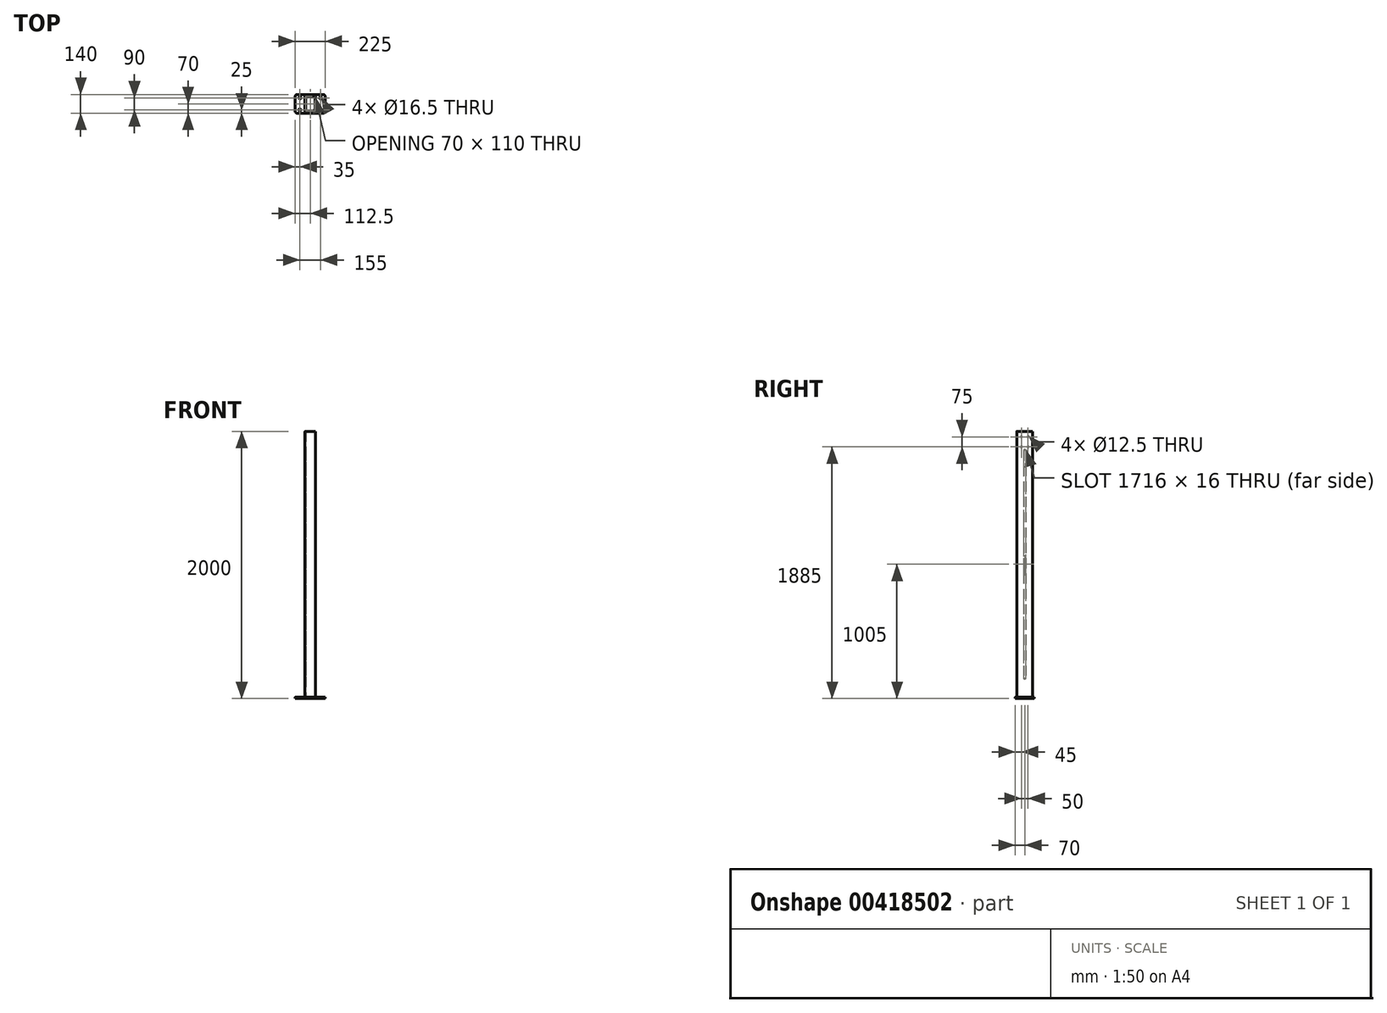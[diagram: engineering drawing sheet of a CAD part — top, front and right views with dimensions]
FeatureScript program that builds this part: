
annotation { "Feature Type Name" : "Feature", "Feature Type Description" : "" }
export const myFeature = defineFeature(function(context is Context, id is Id, definition is map)
    precondition{}
    {
        {
            var Q0;
            Q0=qCreatedBy(makeId("Top.planeOp"),FACE);
            var sketch = newSketch(context, id + "F0", { "sketchPlane" : qUnion([Q0])});
            skLineSegment(sketch, "E0.bottom", {"start": v(97.5, 70) * mm, "end": v(-97.5, 70) * mm});
            skLineSegment(sketch, "E0.top", {"start": v(97.5, -70) * mm, "end": v(-97.5, -70) * mm});
            skLineSegment(sketch, "E0.left", {"start": v(112.5, 55) * mm, "end": v(112.5, -55) * mm});
            skLineSegment(sketch, "E0.right", {"start": v(-112.5, 55) * mm, "end": v(-112.5, -55) * mm});
            skPoint(sketch, "E0.middle", {"position": v(0, 0) * mm});
            skPoint(sketch, "E1.visualSharp", {"position": v(-112.5, 70) * mm});
            skArc(sketch, "E1.filletArc", {"start": v(-97.5, 70) * mm, "mid": v(-108.1, 65.6) * mm, "end": v(-112.5, 55) * mm});
            skPoint(sketch, "E2.visualSharp", {"position": v(-112.5, -70) * mm});
            skArc(sketch, "E2.filletArc", {"start": v(-112.5, -55) * mm, "mid": v(-108.1, -65.6) * mm, "end": v(-97.5, -70) * mm});
            skPoint(sketch, "E3.visualSharp", {"position": v(112.5, 70) * mm});
            skArc(sketch, "E3.filletArc", {"start": v(112.5, 55) * mm, "mid": v(108.1, 65.6) * mm, "end": v(97.5, 70) * mm});
            skPoint(sketch, "E4.visualSharp", {"position": v(112.5, -70) * mm});
            skArc(sketch, "E4.filletArc", {"start": v(97.5, -70) * mm, "mid": v(108.1, -65.6) * mm, "end": v(112.5, -55) * mm});
            skCircle(sketch, "E5", {"center": v(-77.5, 45) * mm, "radius": 8.25 * mm});
            skLineSegment(sketch, "E6", {"start": v(-112.5, 0) * mm, "end": v(0, 0) * mm, "construction": true});
            skLineSegment(sketch, "E7", {"start": v(0, 0) * mm, "end": v(0, 70) * mm, "construction": true});
            skCircle(sketch, "E8.MirrorC", {"center": v(77.5, 45) * mm, "radius": 8.25 * mm});
            skCircle(sketch, "E9.MirrorC", {"center": v(77.5, -45) * mm, "radius": 8.25 * mm});
            skCircle(sketch, "E10.MirrorC", {"center": v(-77.5, -45) * mm, "radius": 8.25 * mm});
            skSolve(sketch);
        }
        {
            var Q0;
            Q0 = qSketchRegion(id + "F0", true);
            extrude(context, id + "F1", {"entities" : qUnion([Q0]), "depth" : 10 * mm});
        }
        {
            var Q0;
            Q0=makeQuery(id+"F1.opExtrude","CAP_FACE",FACE,{"disambiguationData":[OSD([sQuery(id+"F0.wireOp",EDGE,"E0.bottom"),sQuery(id+"F0.wireOp",EDGE,"E0.top"),sQuery(id+"F0.wireOp",EDGE,"E0.left"),sQuery(id+"F0.wireOp",EDGE,"E0.right"),sQuery(id+"F0.wireOp",EDGE,"E1.filletArc"),sQuery(id+"F0.wireOp",EDGE,"E2.filletArc"),sQuery(id+"F0.wireOp",EDGE,"E3.filletArc"),sQuery(id+"F0.wireOp",EDGE,"E4.filletArc"),sQuery(id+"F0.wireOp",EDGE,"E5"),sQuery(id+"F0.wireOp",EDGE,"E8.MirrorC"),sQuery(id+"F0.wireOp",EDGE,"E9.MirrorC"),sQuery(id+"F0.wireOp",EDGE,"E10.MirrorC")])],"isStart":false});
            var sketch = newSketch(context, id + "F2", { "sketchPlane" : qUnion([Q0])});
            skLineSegment(sketch, "E11.bottom", {"start": v(30, 60) * mm, "end": v(-30, 60) * mm});
            skLineSegment(sketch, "E11.top", {"start": v(30, -60) * mm, "end": v(-30, -60) * mm});
            skLineSegment(sketch, "E11.left", {"start": v(40, 50) * mm, "end": v(40, -50) * mm});
            skLineSegment(sketch, "E11.right", {"start": v(-40, 50) * mm, "end": v(-40, -50) * mm});
            skPoint(sketch, "E11.middle", {"position": v(0, 0) * mm});
            skPoint(sketch, "E12.visualSharp", {"position": v(-40, 60) * mm});
            skArc(sketch, "E12.filletArc", {"start": v(-30, 60) * mm, "mid": v(-37.07, 57.07) * mm, "end": v(-40, 50) * mm});
            skPoint(sketch, "E13.visualSharp", {"position": v(40, 60) * mm});
            skArc(sketch, "E13.filletArc", {"start": v(40, 50) * mm, "mid": v(37.07, 57.07) * mm, "end": v(30, 60) * mm});
            skPoint(sketch, "E14.visualSharp", {"position": v(40, -60) * mm});
            skArc(sketch, "E14.filletArc", {"start": v(30, -60) * mm, "mid": v(37.07, -57.07) * mm, "end": v(40, -50) * mm});
            skPoint(sketch, "E15.visualSharp", {"position": v(-40, -60) * mm});
            skArc(sketch, "E15.filletArc", {"start": v(-40, -50) * mm, "mid": v(-37.07, -57.07) * mm, "end": v(-30, -60) * mm});
            skArc(sketch, "E16.0", {"start": v(-30, 55) * mm, "mid": v(-33.54, 53.54) * mm, "end": v(-35, 50) * mm});
            skLineSegment(sketch, "E16.1", {"start": v(30, 55) * mm, "end": v(-30, 55) * mm});
            skLineSegment(sketch, "E16.2", {"start": v(-35, 50) * mm, "end": v(-35, -50) * mm});
            skArc(sketch, "E16.3", {"start": v(35, 50) * mm, "mid": v(33.54, 53.54) * mm, "end": v(30, 55) * mm});
            skArc(sketch, "E16.4", {"start": v(-35, -50) * mm, "mid": v(-33.54, -53.54) * mm, "end": v(-30, -55) * mm});
            skLineSegment(sketch, "E16.5", {"start": v(30, -55) * mm, "end": v(-30, -55) * mm});
            skArc(sketch, "E16.6", {"start": v(30, -55) * mm, "mid": v(33.54, -53.54) * mm, "end": v(35, -50) * mm});
            skLineSegment(sketch, "E16.7", {"start": v(35, 50) * mm, "end": v(35, -50) * mm});
            skSolve(sketch);
        }
        {
            var Q0;
            Q0 = qSketchRegion(id + "F2", true);
            extrude(context, id + "F3", {"entities" : qUnion([Q0]), "depth" : 1990 * mm});
        }
        {
            var Q0;
            Q0=makeQuery(id+"F3.opExtrude","SWEPT_FACE",FACE,{"disambiguationData":[OSD([sQuery(id+"F2.wireOp",EDGE,"E11.right")])]});
            var sketch = newSketch(context, id + "F4", { "sketchPlane" : qUnion([Q0])});
            skLineSegment(sketch, "E17", {"start": v(0, 1855) * mm, "end": v(0, 155) * mm, "construction": true});
            skArc(sketch, "E18.0.startCap", {"start": v(-8, 1855) * mm, "mid": v(0, 1863) * mm, "end": v(8, 1855) * mm});
            skArc(sketch, "E18.0.endCap", {"start": v(8, 155) * mm, "mid": v(0, 147) * mm, "end": v(-8, 155) * mm});
            skLineSegment(sketch, "E18.0.left", {"start": v(8, 1855) * mm, "end": v(8, 155) * mm});
            skLineSegment(sketch, "E18.0.right", {"start": v(-8, 1855) * mm, "end": v(-8, 155) * mm});
            skCircle(sketch, "E19", {"center": v(-25, 1960) * mm, "radius": 6.25 * mm});
            skCircle(sketch, "E20.0.1.0", {"center": v(-25, 1885) * mm, "radius": 6.25 * mm});
            skLineSegment(sketch, "E20.direction1", {"start": v(-25, 1960) * mm, "end": v(0, 1960) * mm, "construction": true});
            skLineSegment(sketch, "E20.direction2", {"start": v(-25, 1960) * mm, "end": v(-25, 1885) * mm, "construction": true});
            skCircle(sketch, "E21.MirrorC", {"center": v(25, 1960) * mm, "radius": 6.25 * mm});
            skCircle(sketch, "E22.MirrorC", {"center": v(25, 1885) * mm, "radius": 6.25 * mm});
            skSolve(sketch);
        }
        {
            var Q0;
            Q0 = qSketchRegion(id + "F4", true);
            extrude(context, id + "F5", {"entities" : qUnion([Q0]), "operationType" : NewBodyOperationType.REMOVE, "endBound" : BoundingType.UP_TO_NEXT, "oppositeDirection" : true, "depth" : 25 * mm});
        }
    });
